# Revit family: Trane_TVR_Indoor_Wall mounted_4TVW0007(09)EF000AA(2nd DC)
name_source: partatom
category: Equipamento mecânico
units: mm (PartAtom-declared; Revit-internal decimal feet)

## family parameters
Com base no plano de trabalho = Não
Compartilhado = Não
Corte com vazios quando carregada = Não
Cota do conector redondo = Utilizar diâmetro
Número OmniClass = 23.75.00.00
Ponto de cálculo do ambiente = Não
Sempre na vertical = Sim
Tipo de parte = Normal
Título OmniClass = Climate Control (HVAC)

## types (2) — shared parameters
Condensation = air
Cooling Power Input = 28 W
Depth = 203  [stored 0.66601 ft]
Descrição = High efficiency air cooled
Fabricante = Trane
Gas = R410a
Gas pipe = 12.7  [stored 0.0416667 ft]
Heating Power Input = 28 W
Height = 280
Installation = Indoor installation
Liquid pipe = 6.35  [stored 0.0208333 ft]
Machine material = Galvanized Steel
Maximum Fuse Amps = 15 A
Minimum Circuit Amps = 0 A
Panel color = S1022
Power supply = 220-240V ~50/60Hz
Series = TVR ULTRA
URL = https://www.trane.com
Width = 835  [stored 2.7395 ft]
zero-valued in all types: clearance access behind, clearance access front, clearance access left, clearance access right

## per-type parameters (varying)
| type | Air  Flow | Cooling Capacity | Heating Capacity | Net Weight |
| 4TVW0009EF000AA | 417/402/386/370/353/338/316 m3/h | 3 kW | 3 kW | 9.50 kg |
| 4TVW0007EF000AA | 422/411/402/393/380/368/356 m3/h | 2 kW | 2 kW | 8.40 kg |

note: column(s) folded — value = type name in every type: Modelo

note: [stored X ft] marks values corroborated as IEEE doubles in the binary element streams (Revit-internal decimal feet)
